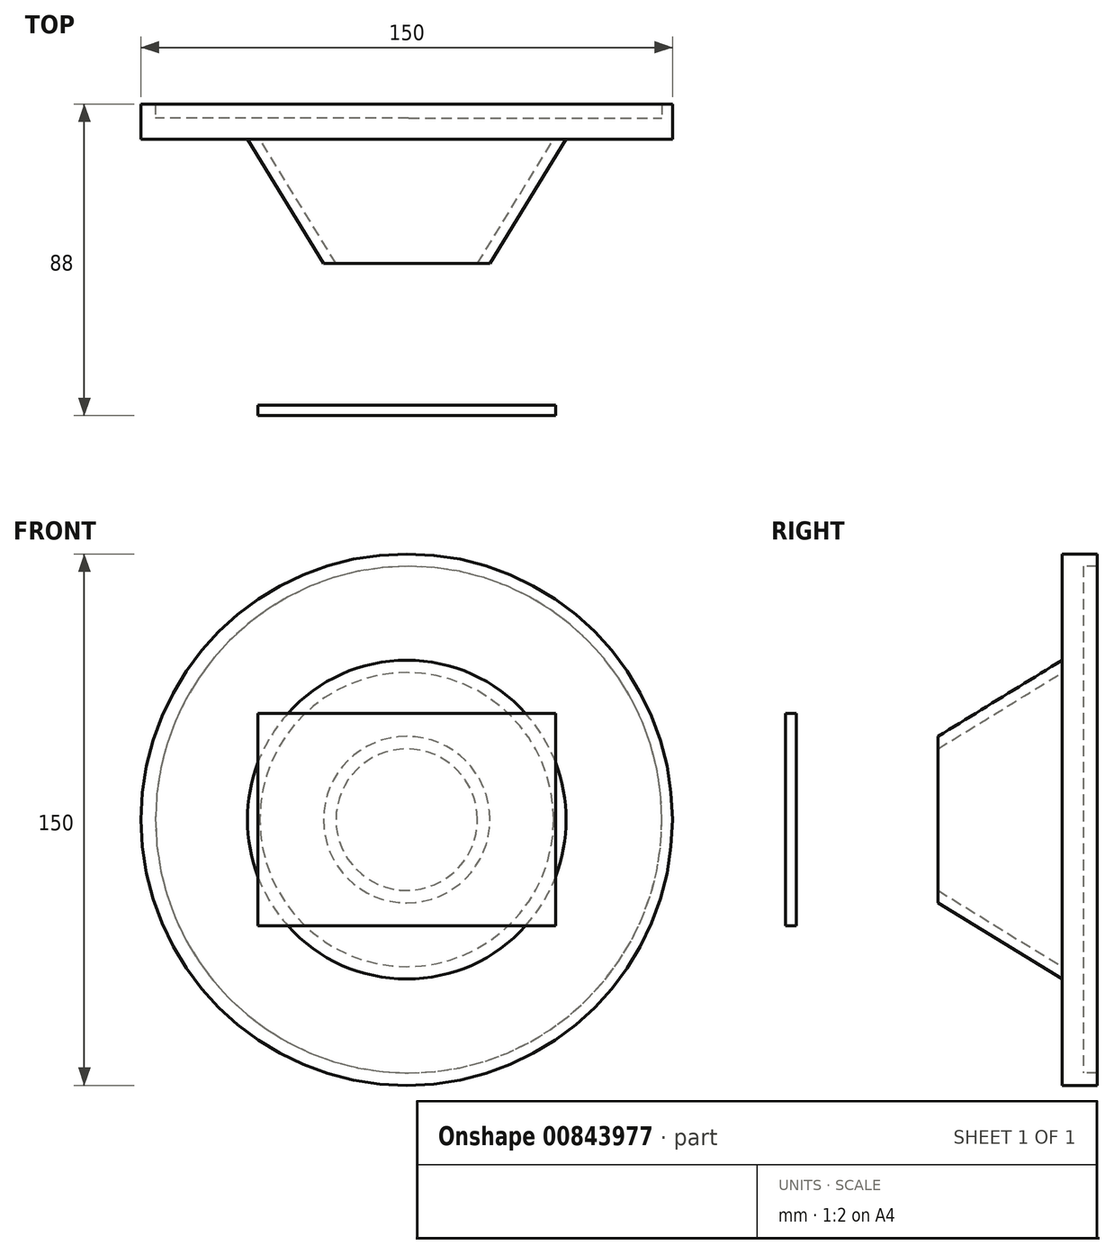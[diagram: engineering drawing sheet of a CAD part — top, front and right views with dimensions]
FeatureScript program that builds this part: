
annotation { "Feature Type Name" : "Feature", "Feature Type Description" : "" }
export const myFeature = defineFeature(function(context is Context, id is Id, definition is map)
    precondition{}
    {
        {
            var Q0;
            Q0=qCreatedBy(makeId("Top.planeOp"),FACE);
            var sketch = newSketch(context, id + "F0", { "sketchPlane" : qUnion([Q0])});
            skLineSegment(sketch, "E0.bottom", {"start": v(-23.5, 0) * mm, "end": v(23.5, 0) * mm});
            skLineSegment(sketch, "E0.top", {"start": v(-23.5, -40) * mm, "end": v(23.5, -40) * mm});
            skLineSegment(sketch, "E0.left", {"start": v(-23.5, 0) * mm, "end": v(-23.5, -40) * mm});
            skLineSegment(sketch, "E0.right", {"start": v(23.5, 0) * mm, "end": v(23.5, -40) * mm});
            skPoint(sketch, "E0.middle", {"position": v(0, -20) * mm});
            skLineSegment(sketch, "E1.bottom", {"start": v(-42, -40) * mm, "end": v(42, -40) * mm});
            skLineSegment(sketch, "E1.top", {"start": v(-42, -43) * mm, "end": v(42, -43) * mm});
            skLineSegment(sketch, "E1.left", {"start": v(-42, -40) * mm, "end": v(-42, -43) * mm});
            skLineSegment(sketch, "E1.right", {"start": v(42, -40) * mm, "end": v(42, -43) * mm});
            skPoint(sketch, "E1.middle", {"position": v(0, -41.5) * mm});
            skPoint(sketch, "E1.middle.positionSnap0", {"position": v(0, -40) * mm});
            skPoint(sketch, "E1.centerSnap0", {"position": v(0, -40) * mm});
            skLineSegment(sketch, "E2", {"start": v(-23.5, 0) * mm, "end": v(-45, 35) * mm});
            skLineSegment(sketch, "E3", {"start": v(23.5, 0) * mm, "end": v(45, 35) * mm});
            skPoint(sketch, "E4.middle", {"position": v(0, 35) * mm});
            skLineSegment(sketch, "E5", {"start": v(75, 35) * mm, "end": v(-75, 35) * mm});
            skLineSegment(sketch, "E6", {"start": v(-75, 35) * mm, "end": v(-75, 45) * mm});
            skLineSegment(sketch, "E7", {"start": v(-75, 45) * mm, "end": v(75, 45) * mm});
            skLineSegment(sketch, "E8", {"start": v(75, 45) * mm, "end": v(75, 35) * mm});
            skLineSegment(sketch, "E9", {"start": v(0, 35) * mm, "end": v(0, 0) * mm});
            skLineSegment(sketch, "E10", {"start": v(0, 45) * mm, "end": v(0, 35) * mm});
            skLineSegment(sketch, "E11", {"start": v(0, 0) * mm, "end": v(0, -40) * mm});
            skLineSegment(sketch, "E12", {"start": v(0, -43) * mm, "end": v(0, -40) * mm});
            skLineSegment(sketch, "E13.0", {"start": v(19.98, 0) * mm, "end": v(41.48, 35) * mm});
            skSolve(sketch);
        }
        {
            var Q0;
            Q0=makeQuery(id+"F0.imprint","IMPRINT",FACE,{"disambiguationData":[TD([[makeQuery(id+"F0.imprint","IMPRINT",EDGE,{"derivedFrom":sQuery(id+"F0.wireOp",EDGE,"E1.top")}),1.0]])]});
            extrude(context, id + "F1", {"entities" : qUnion([Q0]), "endBound" : BoundingType.SYMMETRIC, "depth" : 60 * mm, "offsetDistance" : 25 * mm});
        }
        {
            var Q0;
            {var subQ0=sQuery(id+"F0.wireOp",EDGE,"E3");Q0=makeQuery(id+"F0.imprint","IMPRINT",FACE,{"disambiguationData":[TD([[makeQuery(id+"F0.imprint","IMPRINT",EDGE,{"derivedFrom":subQ0}),1.0]])]});}
            var Q1;
            Q1=sQuery(id+"F0.wireOp",EDGE,"E9");
            revolve(context, id + "F2", {"operationType" : NewBodyOperationType.ADD, "surfaceOperationType" : NewSurfaceOperationType.NEW, "entities" : qUnion([Q0]), "axis" : qUnion([Q1]), "revolveType" : RevolveType.SYMMETRIC, "angle" : 360 * degree});
        }
        {
            var Q0;
            {var subQ1=sQuery(id+"F0.wireOp",EDGE,"E6");Q0=makeQuery(id+"F0.imprint","IMPRINT",FACE,{"disambiguationData":[TD([[makeQuery(id+"F0.imprint","IMPRINT",EDGE,{"derivedFrom":subQ1}),-1.0]])]});}
            var Q1;
            Q1=sQuery(id+"F0.wireOp",EDGE,"E10");
            revolve(context, id + "F3", {"operationType" : NewBodyOperationType.ADD, "surfaceOperationType" : NewSurfaceOperationType.NEW, "entities" : qUnion([Q0]), "axis" : qUnion([Q1]), "revolveType" : RevolveType.SYMMETRIC, "angle" : 360 * degree});
        }
        {
            var Q0;
            Q0=makeQuery(id+"F3.opRevolve","SWEPT_FACE",FACE,{"disambiguationData":[OSD([sQuery(id+"F0.wireOp",EDGE,"E7")])]});
            var sketch = newSketch(context, id + "F4", { "sketchPlane" : qUnion([Q0])});
            skCircle(sketch, "E14", {"center": v(-0.56, 0) * mm, "radius": 71.5 * mm});
            skSolve(sketch);
        }
        {
            var Q0;
            Q0=makeQuery(id+"F4.imprint","IMPRINT",FACE,{"disambiguationData":[TD([[makeQuery(id+"F4.imprint","IMPRINT",EDGE,{"derivedFrom":sQuery(id+"F4.wireOp",EDGE,"E14")}),1.0]])]});
            var Q1;
            Q1=sQuery(id+"F4.wireOp",EDGE,"E14");
            extrude(context, id + "F5", {"entities" : qUnion([Q0]), "operationType" : NewBodyOperationType.REMOVE, "surfaceEntities" : qUnion([Q1]), "endBound" : BoundingType.SYMMETRIC, "depth" : 8 * mm, "offsetDistance" : 25 * mm});
        }
    });
